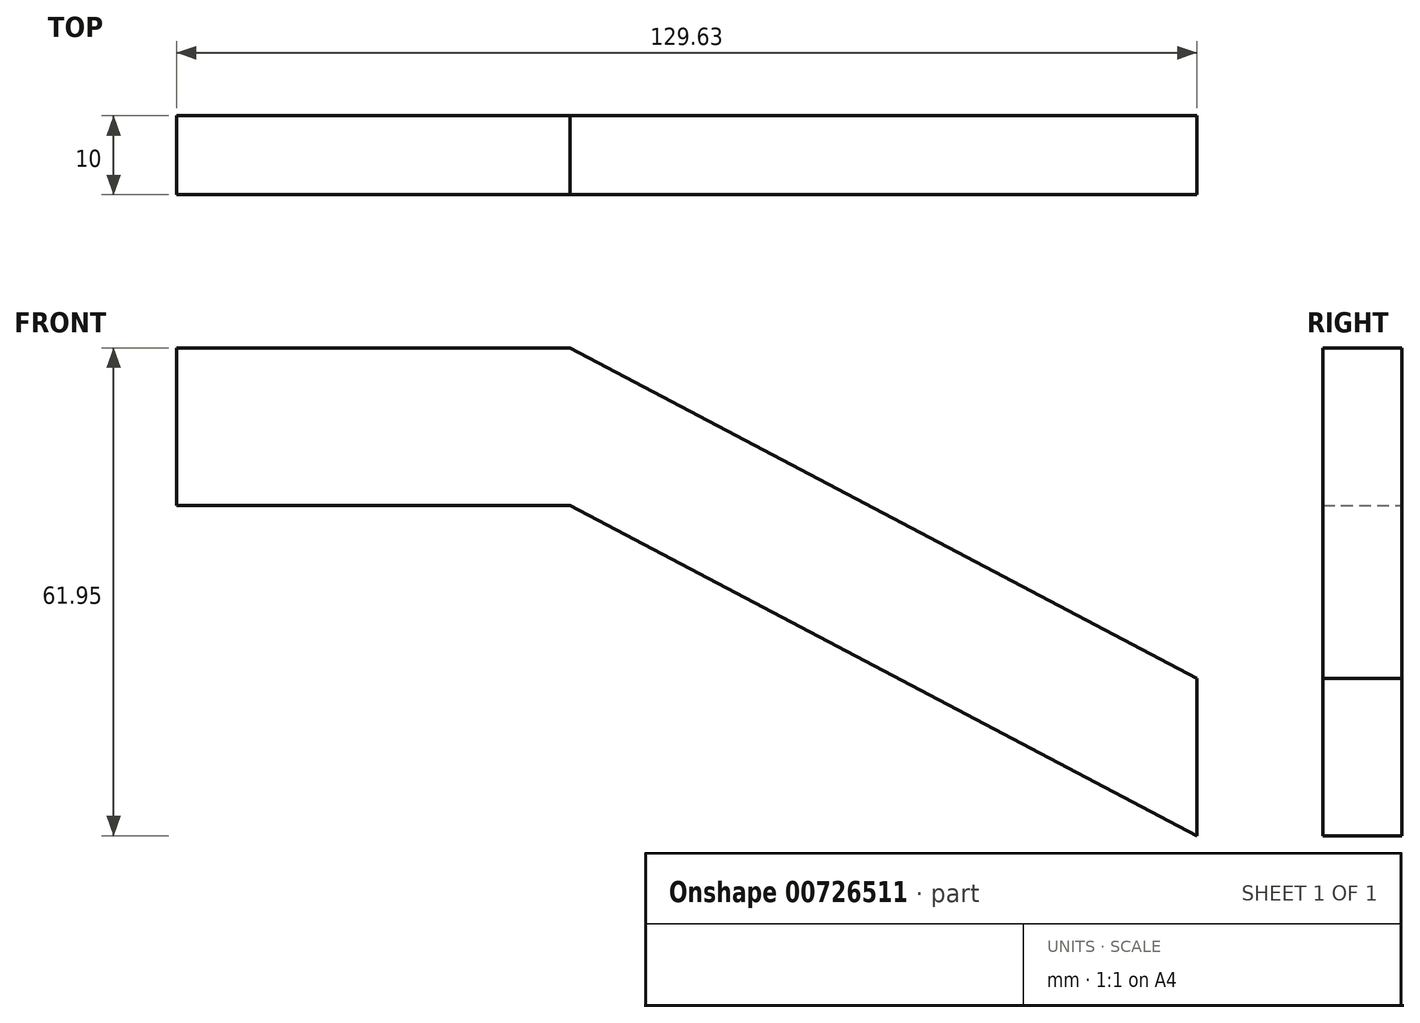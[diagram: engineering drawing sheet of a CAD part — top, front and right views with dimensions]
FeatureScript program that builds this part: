
annotation { "Feature Type Name" : "Feature", "Feature Type Description" : "" }
export const myFeature = defineFeature(function(context is Context, id is Id, definition is map)
    precondition{}
    {
        {
            var Q0;
            Q0=qCreatedBy(makeId("Front.planeOp"),FACE);
            var sketch = newSketch(context, id + "F0", { "sketchPlane" : qUnion([Q0])});
            skLineSegment(sketch, "E0", {"start": v(-63.75, 20) * mm, "end": v(-63.75, 0) * mm});
            skLineSegment(sketch, "E1", {"start": v(-63.75, 20) * mm, "end": v(-13.75, 20) * mm});
            skLineSegment(sketch, "E2", {"start": v(-13.75, 20) * mm, "end": v(65.88, -21.95) * mm});
            skLineSegment(sketch, "E3", {"start": v(-63.75, 0) * mm, "end": v(-13.75, 0) * mm});
            skLineSegment(sketch, "E4", {"start": v(-13.75, 0) * mm, "end": v(65.88, -41.95) * mm});
            skLineSegment(sketch, "E5", {"start": v(65.88, -21.95) * mm, "end": v(65.88, -41.95) * mm});
            skSolve(sketch);
        }
        {
            var Q0;
            Q0 = qSketchRegion(id + "F0", true);
            extrude(context, id + "F1", {"entities" : qUnion([Q0]), "depth" : 10 * mm, "offsetDistance" : 25 * mm});
        }
    });
